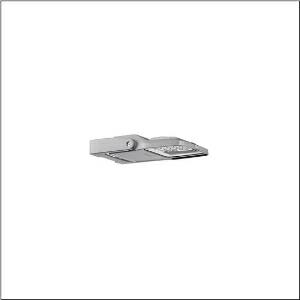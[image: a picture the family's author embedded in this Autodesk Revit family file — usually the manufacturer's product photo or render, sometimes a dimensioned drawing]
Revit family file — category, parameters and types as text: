
# Revit family: floodlight_fl_21_iq_micro___pl43_5xa7762a4a2a_306a
name_source: partatom
category: Lighting Fixtures
units: mm (PartAtom-declared; Revit-internal decimal feet)

## family parameters
Cut with Voids When Loaded = No
Host = Face
Light Source = No
Part Type = Normal
Room Calculation Point = No
Round Connector Dimension = Use Diameter
Shared = No

## types (1)
- --- (1 x LED, 3170 lm, 23.1 W, 4000K)
    Apparent Load = 23 VA
    CIE Flux Codes = 29 80 99 100 100
    Color Rendering = 70
    Color Temperature = 4000K
    Default Elevation = 1800 mm
    Description = Floodlight FL 21 iQ micro, floodlight, primary light control with lens, of PMMA, primary optical cover: protective disc, of toughened safety glass, transparent, light distribution: PL43, light emission: direct distribution, installation type: surface-mounted, LED, High Power LED, rated luminous flux: 3.170lm, luminous efficacy: 137lm/W, light colour: 740, colour temperature: 4000K, control gear: iQ Street-Remote/DALI, control: Auto-Match, Temp-Guard, Night-Set, Smart-Wire, Desk-Remote (wireless, voltage-free reading and setting of iQ features in the workshop via application-optimized NFC function/RFID function), optimised constant luminous flux control (CLO 2.0), Street-Remote, with terminal, 6-pole, mains connection: 220..240V, AC, 50/60Hz, start of lifetime: 23W, end of service life: 24W, reduction: 11W, luminaire housing, of diecast aluminium, powder-coated, Siteco® metallic grey (DB 702S), corrosivity category C5 mid according to DIN EN ISO 12944, suitable for swimming pools, chlorine-resistant, sealing non-destructively replaceable, design bracket, of diecast aluminium, powder-coated, Siteco® metallic grey (DB 702S), protection rating (complete): IP66, insulation class (complete): insulation class II (safety insulation), certification: CE, ENEC, VDE, protection symbol: D, impact resistance: IK07, permissible operating ambient temperature: -40..+40°C, permissible operating ambient temperature for outdoor applications: -40..+50°C, standard: DIN EN 12944, LABS conformity tested according to VDMA 24364:2018-05, packaging unit: 1 piece

Light Distribution: PL43
    Height = 65 mm
    Lamp = 1 x LED
    Lamp Light Flux = 3170 lm
    Lamp Power = 23.1 W
    Lamp count = 1
    Length = 312 mm
    Luminous efficacy = 137 lm/W
    Manufacturer = Siteco
    ModVariant = No
    Model = 5XA7762A4A2A
    Mounting Place = Wall
    Mounting Type = Surface mounted
    Number of Poles = 1
    OnlyDefault = Yes
    Power Factor = 1
    Product Name = Floodlight FL 21 iQ micro | PL43
    Product group = floodlight | wall mounted
    ProductGroupID = 2001
    Protection Class = Protection class II
    Protection Degree = IP 66
    RLX_Detail_Level = 1
    RLX_Emergency_Light_Flux = 0 lm
    RLX_Emergency_Type = 0
    RLX_Emergency_Type_DB = No
    RlxData = <blob elided: 97273 chars, md5=f39f2968>
    Socket = socket
    Standby Power = 0 W
    System Light Flux = 3170 lm
    System Power = 23 W
    Type Comments = factory setting: luminous flux: 100 % | dim-lin: 254 | 455 mA
    Type Image = l_1006878.jpg
    URL = http://relux.com
    VarID = @adj_176504
    Voltage = 0 V
    Weight = 0.00 kg
    Width = 230 mm

## geometry (parser evidence)
native form markers: Blend x4, Sweep x14
no freeform markers — native parametric forms only
